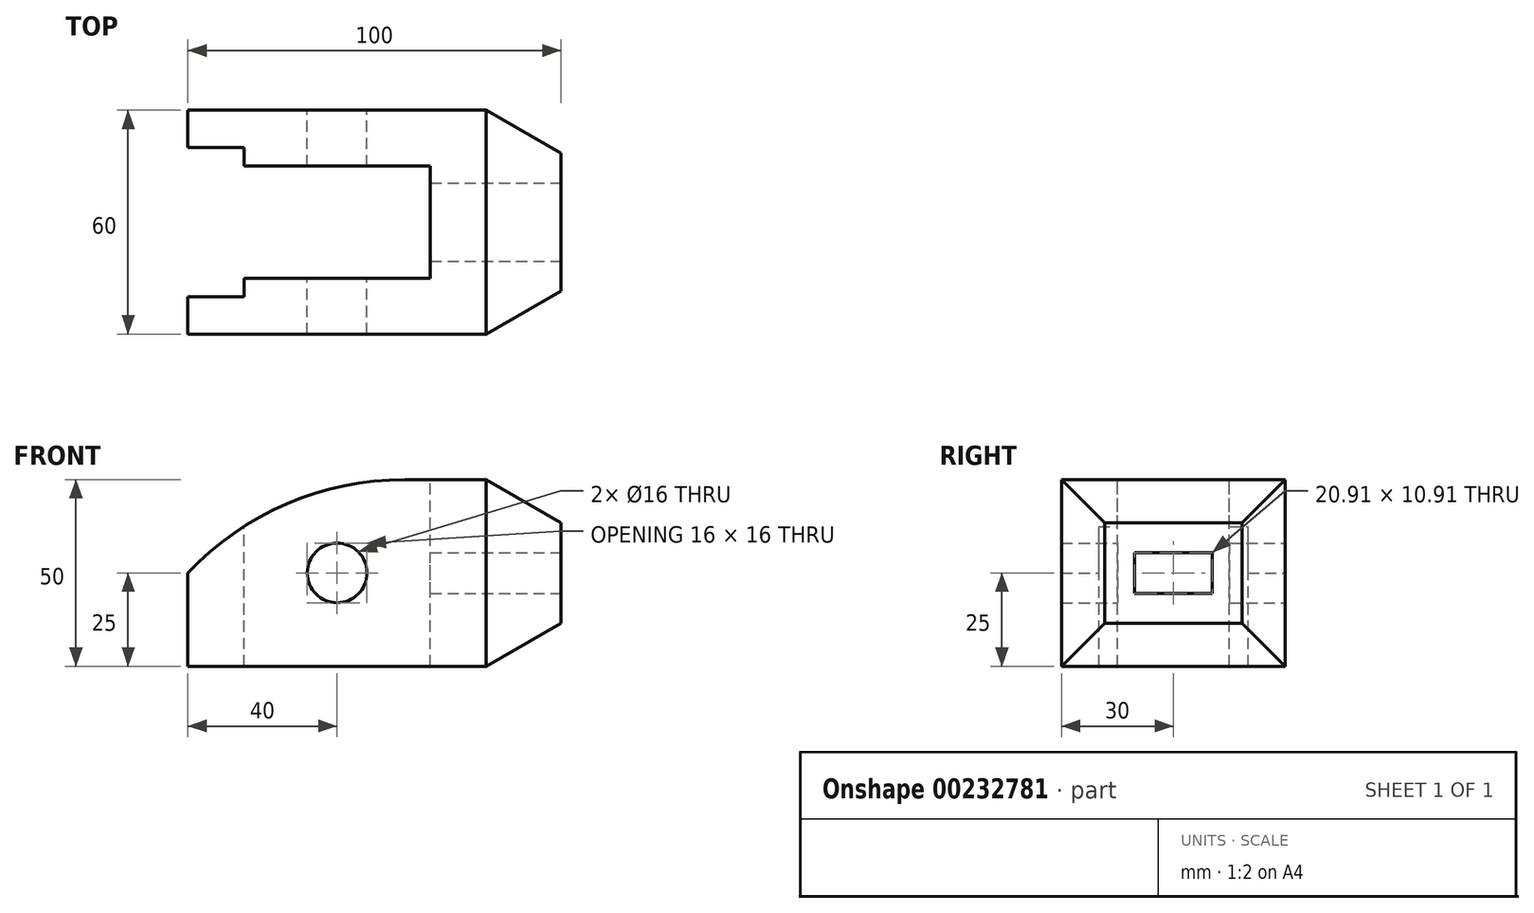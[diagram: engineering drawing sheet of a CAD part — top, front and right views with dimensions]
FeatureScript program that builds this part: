
annotation { "Feature Type Name" : "Feature", "Feature Type Description" : "" }
export const myFeature = defineFeature(function(context is Context, id is Id, definition is map)
    precondition{}
    {
        {
            var Q0;
            Q0=qCreatedBy(makeId("Front.planeOp"),FACE);
            var sketch = newSketch(context, id + "F0", { "sketchPlane" : qUnion([Q0])});
            skCircle(sketch, "E0", {"center": v(0, 0) * mm, "radius": 8 * mm});
            skLineSegment(sketch, "E1", {"start": v(-40, 0) * mm, "end": v(-40, -25) * mm});
            skLineSegment(sketch, "E2", {"start": v(-40, -25) * mm, "end": v(40, -25) * mm});
            skLineSegment(sketch, "E3", {"start": v(40, -25) * mm, "end": v(40, 25) * mm});
            skLineSegment(sketch, "E4", {"start": v(40, 25) * mm, "end": v(18.1, 25) * mm});
            skArc(sketch, "E5", {"start": v(18.1, 25) * mm, "mid": v(-13.53, 18.48) * mm, "end": v(-40, 0) * mm});
            skLineSegment(sketch, "E6", {"start": v(-40, 0) * mm, "end": v(40, 0) * mm, "construction": true});
            skSolve(sketch);
        }
        {
            var Q0;
            Q0=makeQuery(id+"F0.imprint","IMPRINT",FACE,{"disambiguationData":[TD([[makeQuery(id+"F0.imprint","IMPRINT",EDGE,{"derivedFrom":sQuery(id+"F0.wireOp",EDGE,"E0")}),-1.0]])]});
            extrude(context, id + "F1", {"entities" : qUnion([Q0]), "depth" : 60 * mm});
        }
        {
            var Q0;
            Q0=qCreatedBy(makeId("Top.planeOp"),FACE);
            var sketch = newSketch(context, id + "F2", { "sketchPlane" : qUnion([Q0])});
            skLineSegment(sketch, "E7.0.0", {"start": v(18.1, 0) * mm, "end": v(-40, 0) * mm, "construction": true});
            skLineSegment(sketch, "E7.0.2", {"start": v(-40, -60) * mm, "end": v(18.1, -60) * mm, "construction": true});
            skLineSegment(sketch, "E7.0.3", {"start": v(18.1, -60) * mm, "end": v(18.1, 0) * mm, "construction": true});
            skLineSegment(sketch, "E8.0.0", {"start": v(40, 0) * mm, "end": v(18.1, 0) * mm, "construction": true});
            skLineSegment(sketch, "E8.0.1", {"start": v(18.1, 0) * mm, "end": v(18.1, -60) * mm, "construction": true});
            skLineSegment(sketch, "E8.0.2", {"start": v(18.1, -60) * mm, "end": v(40, -60) * mm, "construction": true});
            skLineSegment(sketch, "E8.0.3", {"start": v(40, -60) * mm, "end": v(40, 0) * mm, "construction": true});
            skLineSegment(sketch, "E9.bottom", {"start": v(-25, -50) * mm, "end": v(-40, -50) * mm});
            skLineSegment(sketch, "E9.top", {"start": v(-25, -10) * mm, "end": v(-40, -10) * mm});
            skLineSegment(sketch, "E9.left", {"start": v(-25, -50) * mm, "end": v(-25, -10) * mm});
            skPoint(sketch, "E9.middle", {"position": v(-40, -30) * mm});
            skLineSegment(sketch, "E10", {"start": v(-40, -10) * mm, "end": v(-40, -50) * mm});
            skLineSegment(sketch, "E11.bottom", {"start": v(25, -45) * mm, "end": v(-25, -45) * mm});
            skLineSegment(sketch, "E11.top", {"start": v(25, -15) * mm, "end": v(-25, -15) * mm});
            skLineSegment(sketch, "E11.left", {"start": v(25, -45) * mm, "end": v(25, -15) * mm});
            skPoint(sketch, "E11.middle", {"position": v(-25, -30) * mm});
            skPoint(sketch, "E11.right.end.orphan", {"position": v(-75, -15) * mm});
            skPoint(sketch, "E12.orphan", {"position": v(-75, -45) * mm});
            skLineSegment(sketch, "E13", {"start": v(-25, -45) * mm, "end": v(25, -45) * mm});
            skLineSegment(sketch, "E14", {"start": v(-40, -10) * mm, "end": v(-25, -10) * mm});
            skSolve(sketch);
        }
        {
            var Q0;
            Q0 = qSketchRegion(id + "F2", true);
            extrude(context, id + "F3", {"entities" : qUnion([Q0]), "operationType" : NewBodyOperationType.REMOVE, "endBound" : BoundingType.THROUGH_ALL, "oppositeDirection" : true, "depth" : 25 * mm, "hasSecondDirection" : true, "secondDirectionOppositeDirection" : false, "secondDirectionDepth" : 25 * mm});
        }
        {
            var Q0;
            Q0=makeQuery(id+"F1.opExtrude","SWEPT_FACE",FACE,{"disambiguationData":[OSD([sQuery(id+"F0.wireOp",EDGE,"E3")])]});
            var sketch = newSketch(context, id + "F4", { "sketchPlane" : qUnion([Q0])});
            skLineSegment(sketch, "E15.0.0", {"start": v(0, -25) * mm, "end": v(0, 25) * mm, "construction": true});
            skLineSegment(sketch, "E15.0.1", {"start": v(0, 25) * mm, "end": v(-60, 25) * mm, "construction": true});
            skLineSegment(sketch, "E15.0.2", {"start": v(-60, 25) * mm, "end": v(-60, -25) * mm, "construction": true});
            skLineSegment(sketch, "E15.0.3", {"start": v(-60, -25) * mm, "end": v(0, -25) * mm, "construction": true});
            skLineSegment(sketch, "E16", {"start": v(-30, 25) * mm, "end": v(-30, -25) * mm, "construction": true});
            skPoint(sketch, "E17", {"position": v(-30, 0) * mm});
            skSolve(sketch);
        }
        {
            var Q0;
            {var subQ0=sQuery(id+"F0.wireOp",EDGE,"E3");Q0=makeQuery(id+"F4.imprint","IMPRINT",FACE,{"disambiguationData":[TD([[makeQuery(id+"F4.imprint","IMPRINT",EDGE,{"derivedFrom":makeQuery(id+"F1.opExtrude","CAP_EDGE",EDGE,{"disambiguationData":[OSD([subQ0])],"isStart":true})}),1.0]])]});}
            extrude(context, id + "F5", {"entities" : qUnion([Q0]), "operationType" : NewBodyOperationType.ADD, "depth" : 20 * mm});
        }
        {
            var Q0;
            {var subQ0=sQuery(id+"F0.wireOp",EDGE,"E3");Q0=makeQuery(id+"F5.boolean.opBoolean","MERGE",FACE,{"derivedFrom":[makeQuery(id+"F1.opExtrude","CAP_FACE",FACE,{"disambiguationData":[OSD([sQuery(id+"F0.wireOp",EDGE,"E0"),sQuery(id+"F0.wireOp",EDGE,"E1"),sQuery(id+"F0.wireOp",EDGE,"E2"),subQ0,sQuery(id+"F0.wireOp",EDGE,"E4"),sQuery(id+"F0.wireOp",EDGE,"E5")])],"isStart":false}),makeQuery(id+"F5.opExtrude","SWEPT_FACE",FACE,{"disambiguationData":[OSD([subQ0]),TDD([makeQuery(id+"F4.imprint","IMPRINT",EDGE,{"derivedFrom":makeQuery(id+"F1.opExtrude","CAP_EDGE",EDGE,{"disambiguationData":[OSD([subQ0])],"isStart":false})})])]})]});}
            var sketch = newSketch(context, id + "F6", { "sketchPlane" : qUnion([Q0])});
            skLineSegment(sketch, "E18.0.0", {"start": v(60, 25) * mm, "end": v(18.1, 25) * mm, "construction": true});
            skArc(sketch, "E18.0.1", {"start": v(18.1, 25) * mm, "mid": v(-13.53, 18.48) * mm, "end": v(-40, 0) * mm, "construction": true});
            skLineSegment(sketch, "E18.0.2", {"start": v(-40, 0) * mm, "end": v(-40, -25) * mm, "construction": true});
            skLineSegment(sketch, "E18.0.3", {"start": v(-40, -25) * mm, "end": v(60, -25) * mm, "construction": true});
            skLineSegment(sketch, "E18.0.4", {"start": v(60, -25) * mm, "end": v(60, 25) * mm, "construction": true});
            skLineSegment(sketch, "E19", {"start": v(40, 25) * mm, "end": v(40, -24.29) * mm, "construction": true});
            skLineSegment(sketch, "E20", {"start": v(34.6, 0) * mm, "end": v(74.54, 0) * mm, "construction": true});
            skPoint(sketch, "E20.endSnap0", {"position": v(60, 0) * mm});
            skLineSegment(sketch, "E21", {"start": v(40, 25) * mm, "end": v(60, 13.45) * mm});
            skLineSegment(sketch, "E22", {"start": v(40, -25) * mm, "end": v(60, -13.45) * mm});
            skSolve(sketch);
        }
        {
            var Q0;
            {var subQ0=sQuery(id+"F6.wireOp",EDGE,"E21");Q0=makeQuery(id+"F6.imprint","IMPRINT",FACE,{"disambiguationData":[TD([[makeQuery(id+"F6.imprint","IMPRINT",EDGE,{"derivedFrom":subQ0}),1.0]])]});}
            var Q1;
            {var subQ0=sQuery(id+"F6.wireOp",EDGE,"E22");Q1=makeQuery(id+"F6.imprint","IMPRINT",FACE,{"disambiguationData":[TD([[makeQuery(id+"F6.imprint","IMPRINT",EDGE,{"derivedFrom":subQ0}),-1.0]])]});}
            extrude(context, id + "F7", {"entities" : qUnion([Q0, Q1]), "operationType" : NewBodyOperationType.REMOVE, "endBound" : BoundingType.THROUGH_ALL, "oppositeDirection" : true, "depth" : 25 * mm});
        }
        {
            var Q0;
            {var subQ0=sQuery(id+"F0.wireOp",EDGE,"E4");Q0=makeQuery(id+"F5.boolean.opBoolean","MERGE",FACE,{"derivedFrom":[makeQuery(id+"F1.opExtrude","SWEPT_FACE",FACE,{"disambiguationData":[OSD([subQ0])]}),makeQuery(id+"F5.opExtrude","SWEPT_FACE",FACE,{"disambiguationData":[OSD([sQuery(id+"F0.wireOp",EDGE,"E3"),subQ0])]})]});}
            var sketch = newSketch(context, id + "F8", { "sketchPlane" : qUnion([Q0])});
            skLineSegment(sketch, "E23.0.0", {"start": v(40, 0) * mm, "end": v(40, -60) * mm, "construction": true});
            skLineSegment(sketch, "E23.0.1", {"start": v(40, -60) * mm, "end": v(60, -60) * mm, "construction": true});
            skLineSegment(sketch, "E23.0.3", {"start": v(60, 0) * mm, "end": v(40, 0) * mm, "construction": true});
            skLineSegment(sketch, "E24", {"start": v(40, -30) * mm, "end": v(66.62, -30) * mm, "construction": true});
            skPoint(sketch, "E24.endSnap0", {"position": v(60, -30) * mm});
            skLineSegment(sketch, "E25", {"start": v(40, -60) * mm, "end": v(60, -48.45) * mm});
            skLineSegment(sketch, "E26", {"start": v(40, 0) * mm, "end": v(60, -11.55) * mm});
            skLineSegment(sketch, "E27", {"start": v(40, 0) * mm, "end": v(60, 0) * mm});
            skLineSegment(sketch, "E28", {"start": v(60, -48.45) * mm, "end": v(60, -60) * mm});
            skLineSegment(sketch, "E29", {"start": v(40, -60) * mm, "end": v(60, -60) * mm});
            skLineSegment(sketch, "E30", {"start": v(60, 0) * mm, "end": v(60, -11.55) * mm});
            skSolve(sketch);
        }
        {
            var Q0;
            Q0=makeQuery(id+"F8.imprint","IMPRINT",FACE,{"disambiguationData":[TD([[makeQuery(id+"F8.imprint","IMPRINT",EDGE,{"derivedFrom":sQuery(id+"F8.wireOp",EDGE,"E26")}),1.0]])]});
            var Q1;
            Q1=makeQuery(id+"F8.imprint","IMPRINT",FACE,{"disambiguationData":[TD([[makeQuery(id+"F8.imprint","IMPRINT",EDGE,{"derivedFrom":sQuery(id+"F8.wireOp",EDGE,"E25")}),-1.0]])]});
            extrude(context, id + "F9", {"entities" : qUnion([Q0, Q1]), "operationType" : NewBodyOperationType.REMOVE, "endBound" : BoundingType.THROUGH_ALL, "oppositeDirection" : true, "depth" : 25 * mm});
        }
        {
            var Q0;
            Q0=makeQuery(id+"F5.opExtrude","CAP_FACE",FACE,{"disambiguationData":[OSD([sQuery(id+"F0.wireOp",EDGE,"E2"),sQuery(id+"F0.wireOp",EDGE,"E3"),sQuery(id+"F0.wireOp",EDGE,"E4")])],"isStart":false});
            var sketch = newSketch(context, id + "F10", { "sketchPlane" : qUnion([Q0])});
            skLineSegment(sketch, "E31.0.0", {"start": v(-48.45, 13.45) * mm, "end": v(-48.45, -13.45) * mm, "construction": true});
            skLineSegment(sketch, "E31.0.1", {"start": v(-48.45, -13.45) * mm, "end": v(-11.55, -13.45) * mm, "construction": true});
            skLineSegment(sketch, "E31.0.2", {"start": v(-11.55, -13.45) * mm, "end": v(-11.55, 13.45) * mm, "construction": true});
            skLineSegment(sketch, "E31.0.3", {"start": v(-11.55, 13.45) * mm, "end": v(-48.45, 13.45) * mm, "construction": true});
            skLineSegment(sketch, "E32.bottom", {"start": v(-19.55, -5.45) * mm, "end": v(-40.45, -5.45) * mm});
            skLineSegment(sketch, "E32.top", {"start": v(-19.55, 5.45) * mm, "end": v(-40.45, 5.45) * mm});
            skLineSegment(sketch, "E32.left", {"start": v(-19.55, -5.45) * mm, "end": v(-19.55, 5.45) * mm});
            skLineSegment(sketch, "E32.right", {"start": v(-40.45, -5.45) * mm, "end": v(-40.45, 5.45) * mm});
            skPoint(sketch, "E32.middle", {"position": v(-30, 0) * mm});
            skSolve(sketch);
        }
        {
            var Q0;
            Q0=makeQuery(id+"F10.imprint","IMPRINT",FACE,{"disambiguationData":[TD([[makeQuery(id+"F10.imprint","IMPRINT",EDGE,{"derivedFrom":sQuery(id+"F10.wireOp",EDGE,"E32.bottom")}),-1.0]])]});
            extrude(context, id + "F11", {"entities" : qUnion([Q0]), "operationType" : NewBodyOperationType.REMOVE, "endBound" : BoundingType.THROUGH_ALL, "oppositeDirection" : true, "depth" : 25 * mm});
        }
    });
